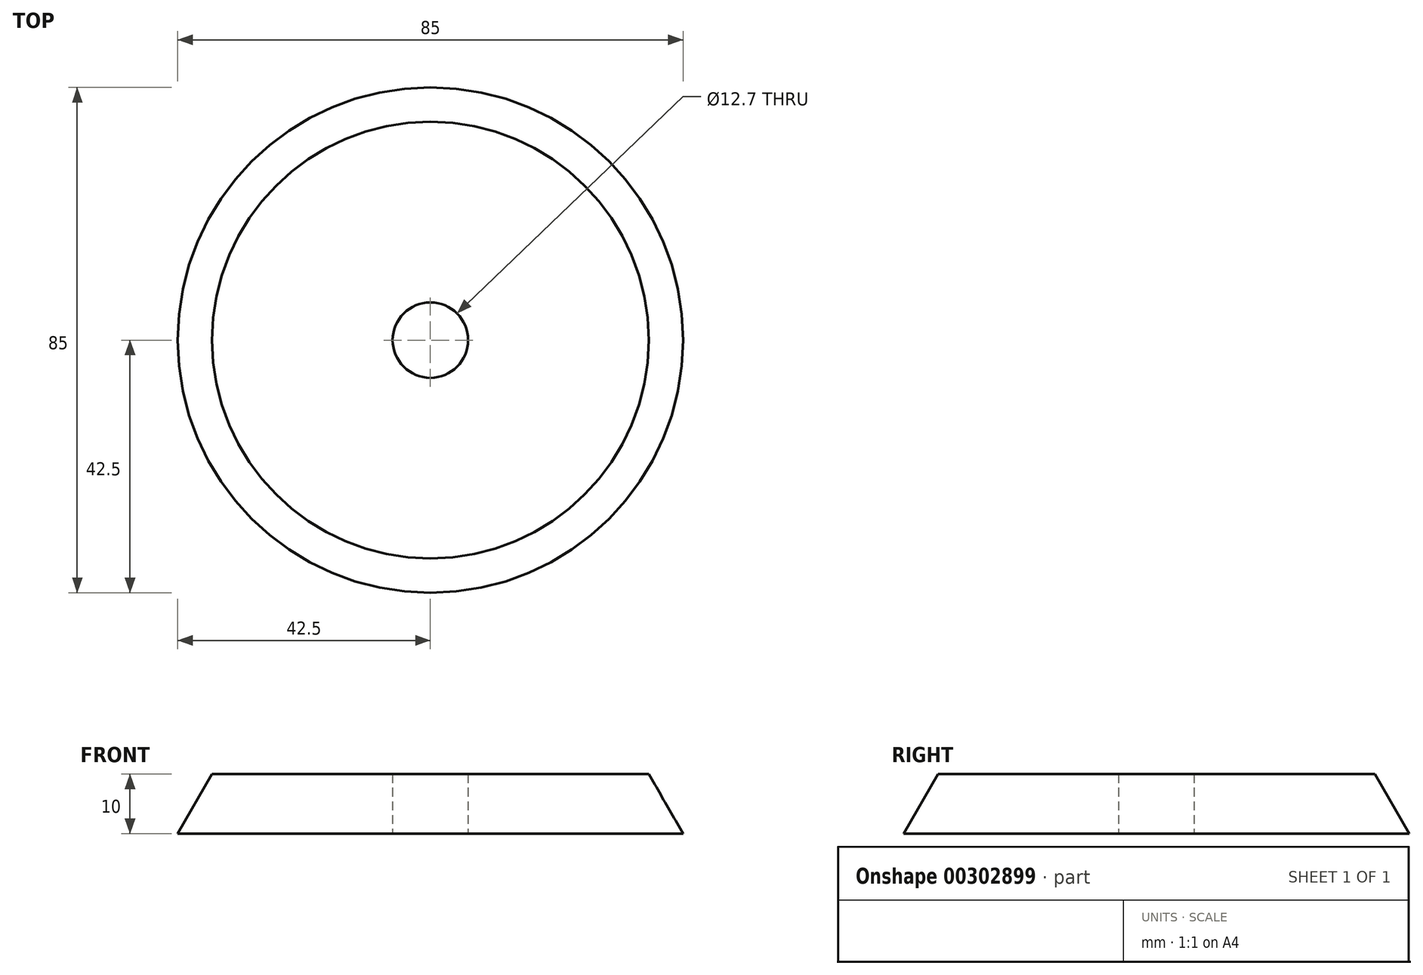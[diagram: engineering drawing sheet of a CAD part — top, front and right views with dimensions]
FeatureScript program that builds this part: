
annotation { "Feature Type Name" : "Feature", "Feature Type Description" : "" }
export const myFeature = defineFeature(function(context is Context, id is Id, definition is map)
    precondition{}
    {
        {
            var Q0;
            Q0=qCreatedBy(makeId("Top.planeOp"),FACE);
            var sketch = newSketch(context, id + "F0", { "sketchPlane" : qUnion([Q0])});
            skCircle(sketch, "E0", {"center": v(0, 0) * mm, "radius": 42.5 * mm});
            skSolve(sketch);
        }
        {
            var Q0;
            Q0 = qSketchRegion(id + "F0", true);
            extrude(context, id + "F1", {"entities" : qUnion([Q0]), "depth" : 10 * mm, "hasDraft" : true, "draftAngle" : 30 * degree, "draftPullDirection" : true});
        }
        {
            var Q0;
            Q0=qCreatedBy(makeId("Top.planeOp"),FACE);
            var sketch = newSketch(context, id + "F2", { "sketchPlane" : qUnion([Q0])});
            skCircle(sketch, "E1", {"center": v(0, 0) * mm, "radius": 6.35 * mm});
            skSolve(sketch);
        }
        {
            var Q0;
            Q0=makeQuery(id+"F2.imprint","IMPRINT",FACE,{"disambiguationData":[TD([[makeQuery(id+"F2.imprint","IMPRINT",EDGE,{"derivedFrom":sQuery(id+"F2.wireOp",EDGE,"E1")}),1.0]])]});
            extrude(context, id + "F3", {"entities" : qUnion([Q0]), "operationType" : NewBodyOperationType.REMOVE, "endBound" : BoundingType.UP_TO_NEXT, "depth" : 25.4 * mm});
        }
    });
